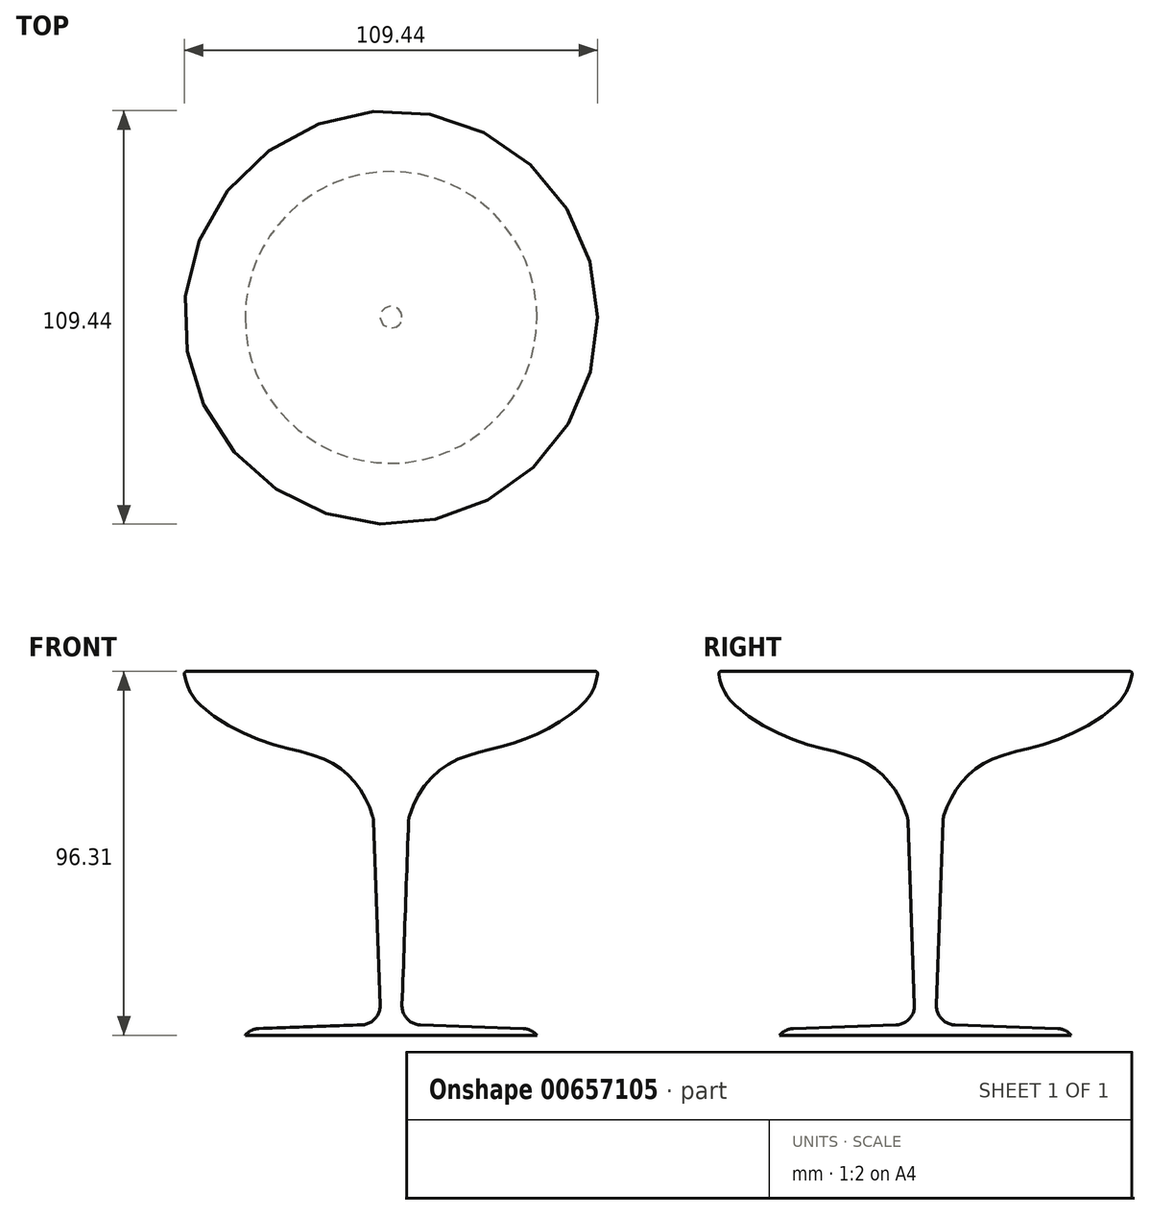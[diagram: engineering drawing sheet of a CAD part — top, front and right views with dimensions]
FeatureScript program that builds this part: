
annotation { "Feature Type Name" : "Feature", "Feature Type Description" : "" }
export const myFeature = defineFeature(function(context is Context, id is Id, definition is map)
    precondition{}
    {
        {
            var Q0;
            Q0=qCreatedBy(makeId("Right.planeOp"),FACE);
            var sketch = newSketch(context, id + "F0", { "sketchPlane" : qUnion([Q0])});
            skFitSpline(sketch, "E0", {"points": [v(-54.85, 41.37) * mm, v(-52, 34.14) * mm, v(-34.02, 22.95) * mm, v(-15.17, 16.82) * mm, v(-4.67, 2.4) * mm], "startDerivative": vector(7.67, -40.33) * mm, "endDerivative": vector(17.9, -68.84) * mm});
            skSolve(sketch);
        }
        {
            var Q0;
            Q0=qCreatedBy(makeId("Right.planeOp"),FACE);
            var sketch = newSketch(context, id + "F1", { "sketchPlane" : qUnion([Q0])});
            skLineSegment(sketch, "E1", {"start": v(-4.67, 2.4) * mm, "end": v(-2.73, -52.03) * mm});
            skLineSegment(sketch, "E2", {"start": v(-2.73, -52.03) * mm, "end": v(-38.62, -53.31) * mm});
            skLineSegment(sketch, "E3", {"start": v(-38.62, -53.31) * mm, "end": v(-38.62, -54.94) * mm});
            skLineSegment(sketch, "E4", {"start": v(-38.62, -54.94) * mm, "end": v(0, -54.94) * mm});
            skSolve(sketch);
        }
        {
            var Q0;
            Q0=qCreatedBy(makeId("Right.planeOp"),FACE);
            var sketch = newSketch(context, id + "F2", { "sketchPlane" : qUnion([Q0])});
            skLineSegment(sketch, "E5", {"start": v(-54.85, 41.37) * mm, "end": v(0, 41.37) * mm});
            skLineSegment(sketch, "E6", {"start": v(0, 41.37) * mm, "end": v(0, -54.94) * mm});
            skSolve(sketch);
        }
        {
            var Q0;
            Q0=qCreatedBy(makeId("Right.planeOp"),FACE);
            var sketch = newSketch(context, id + "F3", { "sketchPlane" : qUnion([Q0])});
            skLineSegment(sketch, "E7", {"start": v(0, -54.94) * mm, "end": v(0, 65.76) * mm});
            skSolve(sketch);
        }
        {
            var Q0;
            Q0=sQuery(id+"F0.wireOp",EDGE,"E0");
            var Q1;
            Q1=sQuery(id+"F2.wireOp",EDGE,"E5");
            var Q2;
            Q2=sQuery(id+"F1.wireOp",EDGE,"E1");
            var Q3;
            Q3=sQuery(id+"F1.wireOp",EDGE,"E2");
            var Q4;
            Q4=sQuery(id+"F1.wireOp",EDGE,"E4");
            var Q5;
            Q5=sQuery(id+"F1.wireOp",EDGE,"E3");
            var Q6;
            Q6=sQuery(id+"F3.wireOp",EDGE,"E7");
            revolve(context, id + "F4", {"bodyType" : ToolBodyType.SURFACE, "operationType" : NewBodyOperationType.ADD, "surfaceEntities" : qUnion([Q0, Q1, Q2, Q3, Q4, Q5]), "axis" : qUnion([Q6]), "revolveType" : RevolveType.FULL});
        }
        {
            var Q0;
            Q0=makeQuery(id+"F4.opRevolve","SWEPT_FACE",FACE,{"disambiguationData":[OSD([sQuery(id+"F1.wireOp",EDGE,"E2")])]});
            var Q1;
            Q1=makeQuery(id+"F4.opRevolve","SWEPT_FACE",FACE,{"disambiguationData":[OSD([sQuery(id+"F1.wireOp",EDGE,"E1")])]});
            fillet(context, id + "F5", {"entities" : qUnion([Q0, Q1]), "radius" : 5.08 * mm, "tangentPropagation" : true, "allowEdgeOverflow" : false});
        }
        {
            var Q0;
            Q0=makeQuery(id+"F4.opRevolve","SWEPT_EDGE",EDGE,{"disambiguationData":[OSD([sQuery(id+"F2.wireOp",VERTEX,"E5.start")])]});
            fillet(context, id + "F6", {"entities" : qUnion([Q0]), "radius" : 0.63 * mm, "tangentPropagation" : true, "allowEdgeOverflow" : false});
        }
    });
